# Revit family: NBS_ConceptCubicleSystems_PnlCbclSym_ForcePrivacy
name_source: partatom
category: Specialty Equipment
units: mm (PartAtom-declared; Revit-internal decimal feet)

## family parameters
Always vertical = Yes
Cut with Voids When Loaded = No
Part Type = Normal
Room Calculation Point = No
Round Connector Dimension = Use Diameter
Shared = No
Work Plane-Based = No

## types (8) — shared parameters
Application = Washrooms in schools, universities, colleges and any other part of the educational sector
AssetType = Fixed
Category = Ss_25_12_60_60:Panel cubicle systems
Description = Force cubicles, ideal for harsh and demanding environments
DoorLeafMaterial = NBS_ConceptCubicleSystems_G059_GrisOrage-Grey
DoorLeafUndercut = 10 mm  [stored 0.0328084 ft]
DurationUnit = year
Features = Black core with a radiused edge, satin anodised aluminium bolt through Ironmongery, vandel and water resistant, floor to ceiling partition for privacy
FittingMaterial = NBS_ConceptCubicleSystems_SatinAnodisedAluminium
Fittings = Satin anodised aluminium
IfcExportAs = IfcFurnitureType
IfcExportType = USERDEFINED
IsBuiltIn = Yes
ManufacturerName = Concept Cubicle Systems
ManufacturerURL = www.conceptcubiclesystems.co.uk
Material = Compact Grade Laminate
ModelReference = Force Privacy Cublicles
NBSCertification = www.nationalbimlibrary.com/cert/kfqmu1qj
NBSDescription = Panel cubicle system
NBSReference = 25-05-60/160
OverDoorPanelMaterial = NBS_ConceptCubicleSystems_G059_GrisOrage-Grey
PanelThickness = 13 mm
Panels = 12 mm compact grade laminate
PartitionMaterial = NBS_ConceptCubicleSystems_G059_GrisOrage-Grey
PilasterMaterial = NBS_ConceptCubicleSystems_G059_GrisOrage-Grey
ProductInformation = https://www.conceptcubiclesystems.co.uk
Size = 1500 x 2600 mm
Status = UNSET
Style = Cubicle
SystemManufacturer = Concept Cubicle Systems
Uniclass2015Code = Ss_25_12_60_60
Uniclass2015Title = Panel cubicle systems
Uniclass2015Version = Systems v1.16
Version = 3
WarrantyDurationUnit = year
zero-valued in all types: PartitionUndercut, PilasterUndercut

## per-type parameters (varying)
| type | BIMObjectName | HasFittingsLeft | HasFittingsRight | HasPartitionLeft | HasPartitionRight | HasPilasterPanelReturnLeft | HasPilasterPanelReturnRight | IsEndCubicle | IsFirstCubicle | IsMiddleCubicle | IsSingleCubicle | IsWallEndEndCubicle | IsWallEndFirstCubicle | IsWallEndSingleCubicle | IsWallToWallSingleCubicle | Name | PilasterPanelReturnLeft | PilasterPanelReturnRight |
| SingleCubicle | NBS_ConceptCubicleSystems_PanelCubicleSystem_ForcePrivacy_SingleCubicle | No | No | Yes | Yes | Yes | Yes | No | No | No | Yes | No | No | No | No | PanelCubicleSystem_ForcePrivacy_SingleCubicle_ConceptCubicleSystems | 6 mm  [stored 0.019685 ft] | 6 mm  [stored 0.019685 ft] |
| WallToWallSingleCubicle | NBS_ConceptCubicleSystems_PanelCubicleSystem_ForcePrivacy_WallToWallSingleCubicle | Yes | Yes | No | No | No | No | No | No | No | No | No | No | No | Yes | PanelCubicleSystem_ForcePrivacy_WallToWallSingleCubicle_ConceptCubicleSystems | 0 mm  [stored 0 ft] | 0 mm  [stored 0 ft] |
| EndCubicle | NBS_ConceptCubicleSystems_PanelCubicleSystem_ForcePrivacy_EndCubicle | No | No | No | Yes | No | Yes | Yes | No | No | No | No | No | No | No | PanelCubicleSystem_ForcePrivacy_EndCubicle_ConceptCubicleSystems | 0 mm  [stored 0 ft] | 6 mm  [stored 0.019685 ft] |
| FirstCubicle | NBS_ConceptCubicleSystems_PanelCubicleSystem_ForcePrivacy_FirstCubicle | No | No | Yes | Yes | Yes | No | No | Yes | No | No | No | No | No | No | PanelCubicleSystem_ForcePrivacy_FirstCubicle_ConceptCubicleSystems | 6 mm  [stored 0.019685 ft] | 0 mm  [stored 0 ft] |
| WallEndFirstCubicle | NBS_ConceptCubicleSystems_PanelCubicleSystem_ForcePrivacy_WallEndFirstCubicle | Yes | No | No | Yes | No | No | No | No | No | No | No | Yes | No | No | PanelCubicleSystem_ForcePrivacy_WallEndFirstCubicle_ConceptCubicleSystems | 0 mm  [stored 0 ft] | 0 mm  [stored 0 ft] |
| WallEndSingleCubicle | NBS_ConceptCubicleSystems_PanelCubicleSystem_ForcePrivacy_WallEndSingleCubicle | Yes | No | No | Yes | No | Yes | No | No | No | No | No | No | Yes | No | PanelCubicleSystem_ForcePrivacy_WallEndSingleCubicle_ConceptCubicleSystems | 0 mm  [stored 0 ft] | 6 mm  [stored 0.019685 ft] |
| MiddleCubicle | NBS_ConceptCubicleSystems_PanelCubicleSystem_ForcePrivacy_MiddleCubicle | No | No | No | Yes | No | No | No | No | Yes | No | No | No | No | No | PanelCubicleSystem_ForcePrivacy_MiddleCubicle_ConceptCubicleSystems | 0 mm  [stored 0 ft] | 0 mm  [stored 0 ft] |
| WallEndEndCubicle | NBS_ConceptCubicleSystems_PanelCubicleSystem_ForcePrivacy_WallEndEndCubicle | No | Yes | No | No | No | No | No | No | No | No | Yes | No | No | No | PanelCubicleSystem_ForcePrivacy_WallEndEndCubicle_ConceptCubicleSystems | 0 mm  [stored 0 ft] | 0 mm  [stored 0 ft] |

note: [stored X ft] marks values corroborated as IEEE doubles in the binary element streams (Revit-internal decimal feet)

## geometry (parser evidence)
native form markers: Sweep x5
no freeform markers — native parametric forms only
